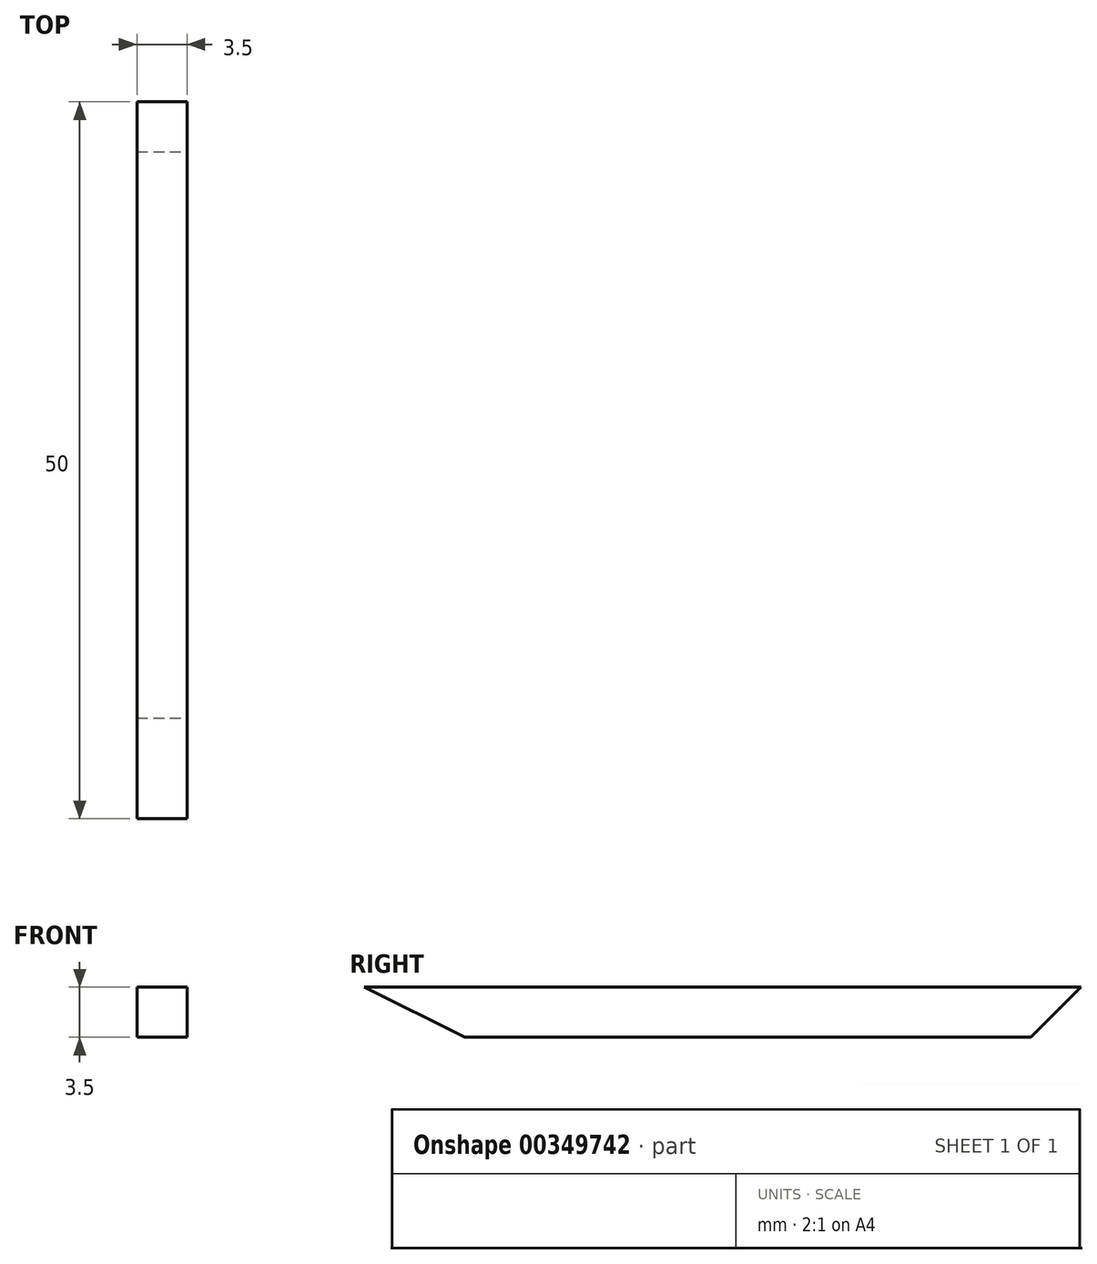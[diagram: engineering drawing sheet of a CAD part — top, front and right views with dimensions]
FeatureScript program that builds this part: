
annotation { "Feature Type Name" : "Feature", "Feature Type Description" : "" }
export const myFeature = defineFeature(function(context is Context, id is Id, definition is map)
    precondition{}
    {
        {
            var Q0;
            Q0=qCreatedBy(makeId("Top.planeOp"),FACE);
            var sketch = newSketch(context, id + "F0", { "sketchPlane" : qUnion([Q0])});
            skLineSegment(sketch, "E0.bottom", {"start": v(1.75, -25) * mm, "end": v(-1.75, -25) * mm});
            skLineSegment(sketch, "E0.top", {"start": v(1.75, 25) * mm, "end": v(-1.75, 25) * mm});
            skLineSegment(sketch, "E0.left", {"start": v(1.75, -25) * mm, "end": v(1.75, 25) * mm});
            skLineSegment(sketch, "E0.right", {"start": v(-1.75, -25) * mm, "end": v(-1.75, 25) * mm});
            skPoint(sketch, "E0.middle", {"position": v(0, 0) * mm});
            skSolve(sketch);
        }
        {
            var Q0;
            Q0=qSketchRegion(id+"F0",true);
            extrude(context, id + "F1", {"entities" : qUnion([Q0]), "depth" : 3.5 * mm});
        }
        {
            var Q0;
            Q0=makeQuery(id+"F1.opExtrude","SWEPT_FACE",FACE,{"disambiguationData":[OSD([sQuery(id+"F0.wireOp",EDGE,"E0.left")])]});
            var sketch = newSketch(context, id + "F2", { "sketchPlane" : qUnion([Q0])});
            skLineSegment(sketch, "E1", {"start": v(-25, 3.5) * mm, "end": v(-18, 0) * mm});
            skLineSegment(sketch, "E2", {"start": v(-18, 0) * mm, "end": v(-25, 0) * mm});
            skLineSegment(sketch, "E3", {"start": v(-25, 0) * mm, "end": v(-25, 3.5) * mm});
            skLineSegment(sketch, "E4", {"start": v(25, 3.5) * mm, "end": v(21.5, 0) * mm});
            skLineSegment(sketch, "E5", {"start": v(21.5, 0) * mm, "end": v(25, 0) * mm});
            skLineSegment(sketch, "E6", {"start": v(25, 0) * mm, "end": v(25, 3.5) * mm});
            skSolve(sketch);
        }
        {
            var Q0;
            Q0=qSketchRegion(id+"F2",true);
            extrude(context, id + "F3", {"entities" : qUnion([Q0]), "operationType" : NewBodyOperationType.REMOVE, "endBound" : BoundingType.THROUGH_ALL, "oppositeDirection" : true, "depth" : 25.4 * mm});
        }
    });
